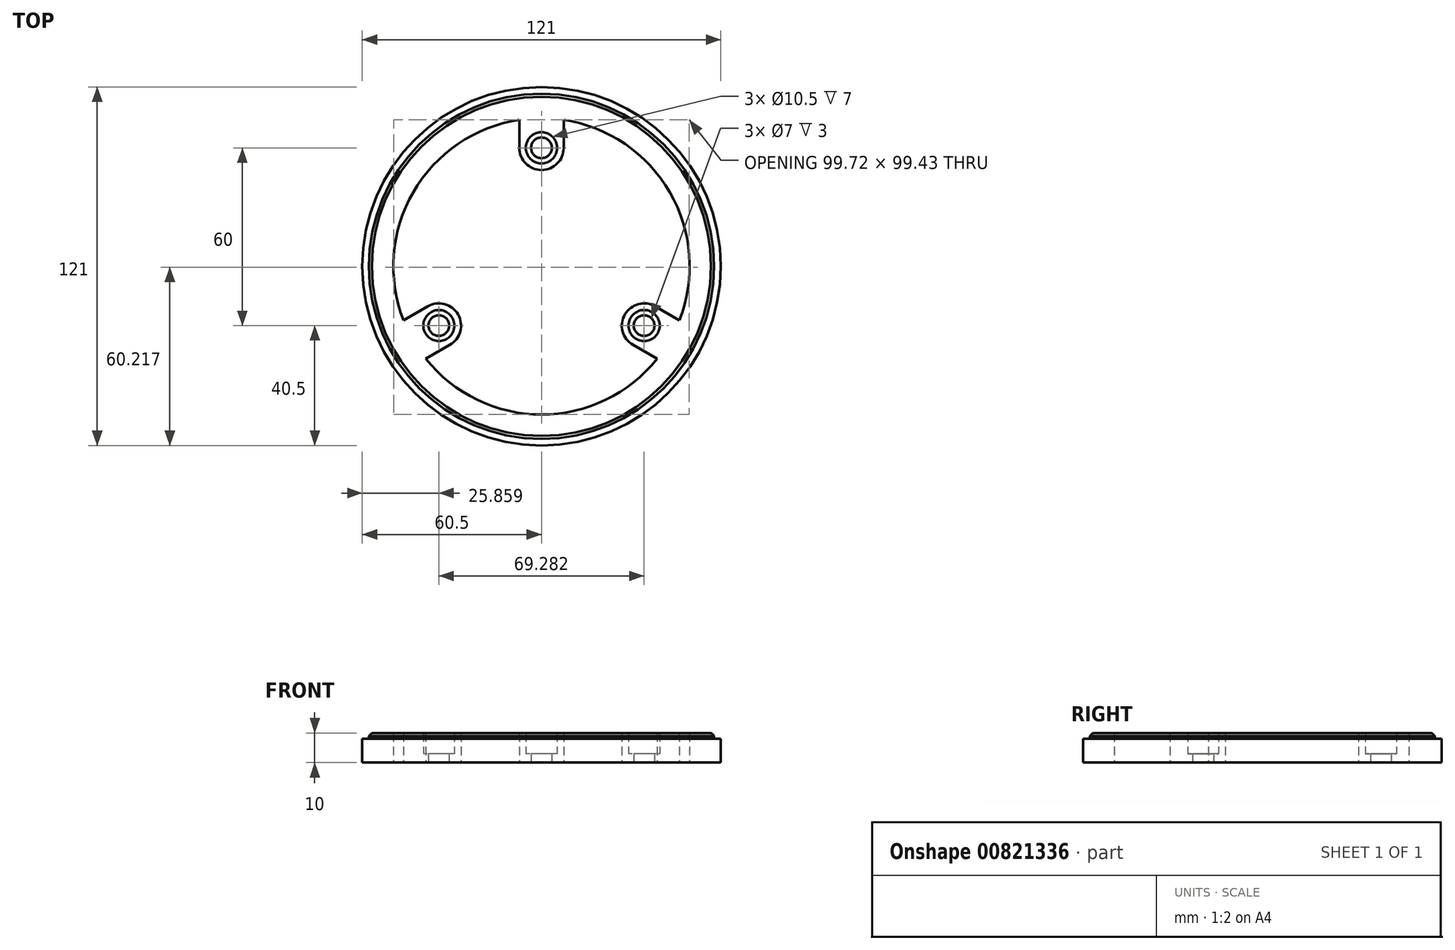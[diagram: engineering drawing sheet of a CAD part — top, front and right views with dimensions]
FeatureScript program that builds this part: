
annotation { "Feature Type Name" : "Feature", "Feature Type Description" : "" }
export const myFeature = defineFeature(function(context is Context, id is Id, definition is map)
    precondition{}
    {
        {
            var Q0;
            Q0=qCreatedBy(makeId("Top.planeOp"),FACE);
            var sketch = newSketch(context, id + "F0", { "sketchPlane" : qUnion([Q0])});
            skCircle(sketch, "E0", {"center": v(0, 0) * mm, "radius": 60.5 * mm});
            skCircle(sketch, "E1", {"center": v(0, 0) * mm, "radius": 50 * mm});
            skCircle(sketch, "E2", {"center": v(0, 0) * mm, "radius": 58.25 * mm});
            skLineSegment(sketch, "E3", {"start": v(0, 50) * mm, "end": v(0, 40) * mm});
            skCircle(sketch, "E4", {"center": v(0, 40) * mm, "radius": 5.25 * mm});
            skCircle(sketch, "E5", {"center": v(0, 40) * mm, "radius": 7.5 * mm});
            skLineSegment(sketch, "E6.bottom", {"start": v(7.5, 57.77) * mm, "end": v(-7.5, 57.77) * mm});
            skLineSegment(sketch, "E6.top", {"start": v(7.5, 22.23) * mm, "end": v(-7.5, 22.23) * mm});
            skLineSegment(sketch, "E6.left", {"start": v(7.5, 57.77) * mm, "end": v(7.5, 22.23) * mm});
            skLineSegment(sketch, "E6.right", {"start": v(-7.5, 57.77) * mm, "end": v(-7.5, 22.23) * mm});
            skCircle(sketch, "E7.1.0", {"center": v(34.64, -20) * mm, "radius": 7.5 * mm});
            skCircle(sketch, "E7.1.1", {"center": v(34.64, -20) * mm, "radius": 5.25 * mm});
            skLineSegment(sketch, "E7.1.2", {"start": v(53.78, -22.39) * mm, "end": v(23, -4.62) * mm});
            skLineSegment(sketch, "E7.1.3", {"start": v(46.28, -35.38) * mm, "end": v(15.5, -17.61) * mm});
            skCircle(sketch, "E7.2.0", {"center": v(-34.64, -20) * mm, "radius": 7.5 * mm});
            skCircle(sketch, "E7.2.1", {"center": v(-34.64, -20) * mm, "radius": 5.25 * mm});
            skLineSegment(sketch, "E7.2.2", {"start": v(-46.28, -35.38) * mm, "end": v(-15.5, -17.61) * mm});
            skLineSegment(sketch, "E7.2.3", {"start": v(-53.78, -22.39) * mm, "end": v(-23, -4.62) * mm});
            skLineSegment(sketch, "E7.anchor1", {"start": v(0, 0) * mm, "end": v(0, 40) * mm, "construction": true});
            skLineSegment(sketch, "E7.anchor2", {"start": v(0, 0) * mm, "end": v(-34.64, -20) * mm, "construction": true});
            skCircle(sketch, "E8", {"center": v(0, 40) * mm, "radius": 3.5 * mm});
            skCircle(sketch, "E9", {"center": v(-34.64, -20) * mm, "radius": 3.5 * mm});
            skCircle(sketch, "E10", {"center": v(34.64, -20) * mm, "radius": 3.5 * mm});
            skSolve(sketch);
        }
        {
            var Q0;
            {var subQ0=sQuery(id+"F0.wireOp",EDGE,"E6.left");var subQ1=sQuery(id+"F0.wireOp",EDGE,"E1");var subQ2=makeQuery(id+"F0.imprint","INTERSECT",VERTEX,{"derivedFrom":[subQ1,subQ0]});Q0=makeQuery(id+"F0.imprint","IMPRINT",FACE,{"disambiguationData":[TD([[makeQuery(id+"F0.imprint","IMPRINT",EDGE,{"disambiguationData":[TD([[subQ2,1.0]])],"derivedFrom":subQ1}),-1.0]])]});}
            var Q1;
            {var subQ0=sQuery(id+"F0.wireOp",EDGE,"E6.bottom");Q1=makeQuery(id+"F0.imprint","IMPRINT",FACE,{"disambiguationData":[TD([[makeQuery(id+"F0.imprint","IMPRINT",EDGE,{"derivedFrom":subQ0}),1.0]])]});}
            var Q2;
            {var subQ0=sQuery(id+"F0.wireOp",EDGE,"E6.right");var subQ1=sQuery(id+"F0.wireOp",EDGE,"E1");var subQ2=makeQuery(id+"F0.imprint","INTERSECT",VERTEX,{"derivedFrom":[subQ1,subQ0]});Q2=makeQuery(id+"F0.imprint","IMPRINT",FACE,{"disambiguationData":[TD([[makeQuery(id+"F0.imprint","IMPRINT",EDGE,{"disambiguationData":[TD([[subQ2,-1.0]])],"derivedFrom":subQ1}),-1.0]])]});}
            var Q3;
            {var subQ0=sQuery(id+"F0.wireOp",EDGE,"E7.2.3");var subQ1=sQuery(id+"F0.wireOp",EDGE,"E1");var subQ2=makeQuery(id+"F0.imprint","INTERSECT",VERTEX,{"derivedFrom":[subQ1,subQ0]});Q3=makeQuery(id+"F0.imprint","IMPRINT",FACE,{"disambiguationData":[TD([[makeQuery(id+"F0.imprint","IMPRINT",EDGE,{"disambiguationData":[TD([[subQ2,-1.0]])],"derivedFrom":subQ1}),-1.0]])]});}
            var Q4;
            {var subQ0=sQuery(id+"F0.wireOp",EDGE,"E7.2.2");var subQ1=sQuery(id+"F0.wireOp",EDGE,"E1");var subQ2=makeQuery(id+"F0.imprint","INTERSECT",VERTEX,{"derivedFrom":[subQ1,subQ0]});Q4=makeQuery(id+"F0.imprint","IMPRINT",FACE,{"disambiguationData":[TD([[makeQuery(id+"F0.imprint","IMPRINT",EDGE,{"disambiguationData":[TD([[subQ2,-1.0]])],"derivedFrom":subQ1}),-1.0]])]});}
            var Q5;
            {var subQ0=sQuery(id+"F0.wireOp",EDGE,"E7.1.3");var subQ1=sQuery(id+"F0.wireOp",EDGE,"E1");var subQ2=makeQuery(id+"F0.imprint","INTERSECT",VERTEX,{"derivedFrom":[subQ1,subQ0]});Q5=makeQuery(id+"F0.imprint","IMPRINT",FACE,{"disambiguationData":[TD([[makeQuery(id+"F0.imprint","IMPRINT",EDGE,{"disambiguationData":[TD([[subQ2,-1.0]])],"derivedFrom":subQ1}),-1.0]])]});}
            var Q6;
            {var subQ0=sQuery(id+"F0.wireOp",EDGE,"E6.bottom");Q6=makeQuery(id+"F0.imprint","IMPRINT",FACE,{"disambiguationData":[TD([[makeQuery(id+"F0.imprint","IMPRINT",EDGE,{"derivedFrom":subQ0}),-1.0]])]});}
            var Q7;
            {var subQ0=sQuery(id+"F0.wireOp",EDGE,"E3");var subQ1=sQuery(id+"F0.wireOp",EDGE,"E1");var subQ2=makeQuery(id+"F0.imprint","INTERSECT",VERTEX,{"derivedFrom":[subQ1,subQ0]});Q7=makeQuery(id+"F0.imprint","IMPRINT",FACE,{"disambiguationData":[TD([[makeQuery(id+"F0.imprint","IMPRINT",EDGE,{"disambiguationData":[TD([[subQ2,1.0]])],"derivedFrom":subQ1}),1.0]])]});}
            var Q8;
            {var subQ0=sQuery(id+"F0.wireOp",EDGE,"E3");var subQ1=sQuery(id+"F0.wireOp",EDGE,"E1");var subQ2=makeQuery(id+"F0.imprint","INTERSECT",VERTEX,{"derivedFrom":[subQ1,subQ0]});Q8=makeQuery(id+"F0.imprint","IMPRINT",FACE,{"disambiguationData":[TD([[makeQuery(id+"F0.imprint","IMPRINT",EDGE,{"disambiguationData":[TD([[subQ2,-1.0]])],"derivedFrom":subQ1}),1.0]])]});}
            var Q9;
            Q9=makeQuery(id+"F0.imprint","IMPRINT",FACE,{"disambiguationData":[TD([[makeQuery(id+"F0.imprint","IMPRINT",EDGE,{"derivedFrom":sQuery(id+"F0.wireOp",EDGE,"E4")}),-1.0]])]});
            var Q10;
            {var subQ0=sQuery(id+"F0.wireOp",EDGE,"E7.1.3");var subQ1=sQuery(id+"F0.wireOp",EDGE,"E1");var subQ2=makeQuery(id+"F0.imprint","INTERSECT",VERTEX,{"derivedFrom":[subQ1,subQ0]});Q10=makeQuery(id+"F0.imprint","IMPRINT",FACE,{"disambiguationData":[TD([[makeQuery(id+"F0.imprint","IMPRINT",EDGE,{"disambiguationData":[TD([[subQ2,-1.0]])],"derivedFrom":subQ1}),1.0]])]});}
            var Q11;
            Q11=makeQuery(id+"F0.imprint","IMPRINT",FACE,{"disambiguationData":[TD([[makeQuery(id+"F0.imprint","IMPRINT",EDGE,{"derivedFrom":sQuery(id+"F0.wireOp",EDGE,"E7.1.1")}),-1.0]])]});
            var Q12;
            Q12=makeQuery(id+"F0.imprint","IMPRINT",FACE,{"disambiguationData":[TD([[makeQuery(id+"F0.imprint","IMPRINT",EDGE,{"derivedFrom":sQuery(id+"F0.wireOp",EDGE,"E7.2.1")}),-1.0]])]});
            var Q13;
            {var subQ0=sQuery(id+"F0.wireOp",EDGE,"E7.2.3");var subQ1=sQuery(id+"F0.wireOp",EDGE,"E1");var subQ2=makeQuery(id+"F0.imprint","INTERSECT",VERTEX,{"derivedFrom":[subQ1,subQ0]});Q13=makeQuery(id+"F0.imprint","IMPRINT",FACE,{"disambiguationData":[TD([[makeQuery(id+"F0.imprint","IMPRINT",EDGE,{"disambiguationData":[TD([[subQ2,-1.0]])],"derivedFrom":subQ1}),1.0]])]});}
            extrude(context, id + "F1", {"entities" : qUnion([Q0, Q1, Q2, Q3, Q4, Q5, Q6, Q7, Q8, Q9, Q10, Q11, Q12, Q13]), "depth" : 10 * mm, "offsetDistance" : 25 * mm});
        }
        {
            var Q0;
            Q0=makeQuery(id+"F0.imprint","IMPRINT",FACE,{"disambiguationData":[TD([[makeQuery(id+"F0.imprint","IMPRINT",EDGE,{"derivedFrom":sQuery(id+"F0.wireOp",EDGE,"E0")}),1.0]])]});
            extrude(context, id + "F2", {"entities" : qUnion([Q0]), "operationType" : NewBodyOperationType.ADD, "depth" : 8 * mm, "offsetDistance" : 25 * mm});
        }
        {
            var Q0;
            Q0=makeQuery(id+"F1.opExtrude","CAP_EDGE",EDGE,{"disambiguationData":[OSD([sQuery(id+"F0.wireOp",EDGE,"E2")])],"isStart":false});
            chamfer(context, id + "F3", {"entities" : qUnion([Q0]), "width" : 1 * mm, "tangentPropagation" : true});
        }
        {
            var Q0;
            Q0=makeQuery(id+"F0.imprint","IMPRINT",FACE,{"disambiguationData":[TD([[makeQuery(id+"F0.imprint","IMPRINT",EDGE,{"derivedFrom":sQuery(id+"F0.wireOp",EDGE,"E4")}),1.0]])]});
            var Q1;
            Q1=makeQuery(id+"F0.imprint","IMPRINT",FACE,{"disambiguationData":[TD([[makeQuery(id+"F0.imprint","IMPRINT",EDGE,{"derivedFrom":sQuery(id+"F0.wireOp",EDGE,"E7.2.1")}),1.0]])]});
            var Q2;
            Q2=makeQuery(id+"F0.imprint","IMPRINT",FACE,{"disambiguationData":[TD([[makeQuery(id+"F0.imprint","IMPRINT",EDGE,{"derivedFrom":sQuery(id+"F0.wireOp",EDGE,"E7.1.1")}),1.0]])]});
            extrude(context, id + "F4", {"entities" : qUnion([Q0, Q1, Q2]), "operationType" : NewBodyOperationType.ADD, "depth" : 3 * mm, "offsetDistance" : 25 * mm});
        }
    });
